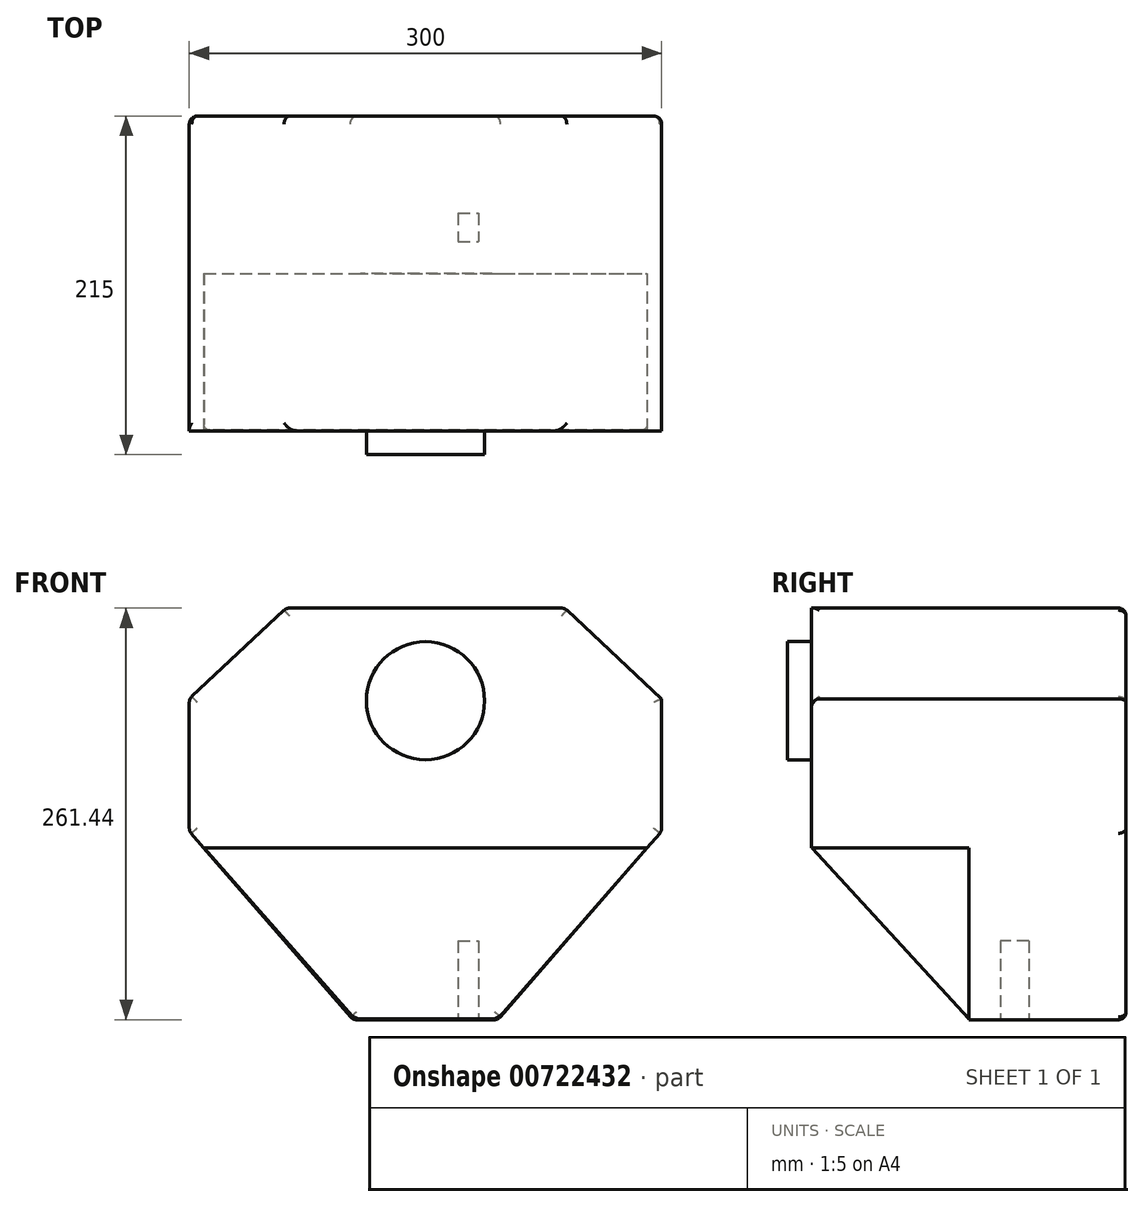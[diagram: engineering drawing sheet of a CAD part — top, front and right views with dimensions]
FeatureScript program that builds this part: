
annotation { "Feature Type Name" : "Feature", "Feature Type Description" : "" }
export const myFeature = defineFeature(function(context is Context, id is Id, definition is map)
    precondition{}
    {
        {
            var Q0;
            Q0=qCreatedBy(makeId("Front.planeOp"),FACE);
            var sketch = newSketch(context, id + "F0", { "sketchPlane" : qUnion([Q0])});
            skLineSegment(sketch, "E0.bottom", {"start": v(-150, -42) * mm, "end": v(150, -42) * mm});
            skLineSegment(sketch, "E0.top", {"start": v(-150, 42) * mm, "end": v(150, 42) * mm});
            skLineSegment(sketch, "E0.left", {"start": v(-150, -42) * mm, "end": v(-150, 42) * mm});
            skLineSegment(sketch, "E0.right", {"start": v(150, -42) * mm, "end": v(150, 42) * mm});
            skPoint(sketch, "E0.middle", {"position": v(0, 0) * mm});
            skLineSegment(sketch, "E1.bottom", {"start": v(-88.3, -15.66) * mm, "end": v(88.3, -15.66) * mm});
            skLineSegment(sketch, "E1.top", {"start": v(-88.3, 99.65) * mm, "end": v(88.3, 99.65) * mm});
            skLineSegment(sketch, "E1.left", {"start": v(-88.3, -15.66) * mm, "end": v(-88.3, 99.65) * mm});
            skLineSegment(sketch, "E1.right", {"start": v(88.3, -15.66) * mm, "end": v(88.3, 99.65) * mm});
            skPoint(sketch, "E1.middle", {"position": v(0, 42) * mm});
            skLineSegment(sketch, "E2.bottom", {"start": v(-46.14, -161.8) * mm, "end": v(46.14, -161.8) * mm});
            skLineSegment(sketch, "E2.top", {"start": v(-46.14, 77.8) * mm, "end": v(46.14, 77.8) * mm});
            skLineSegment(sketch, "E2.left", {"start": v(-46.14, -161.8) * mm, "end": v(-46.14, 77.8) * mm});
            skLineSegment(sketch, "E2.right", {"start": v(46.14, -161.8) * mm, "end": v(46.14, 77.8) * mm});
            skPoint(sketch, "E2.middle", {"position": v(0, -42) * mm});
            skLineSegment(sketch, "E3", {"start": v(-150, -42) * mm, "end": v(-46.14, -161.8) * mm});
            skLineSegment(sketch, "E4", {"start": v(46.14, -161.8) * mm, "end": v(150, -42) * mm});
            skLineSegment(sketch, "E5", {"start": v(-150, 42) * mm, "end": v(-88.3, 99.65) * mm});
            skLineSegment(sketch, "E6", {"start": v(150, 42) * mm, "end": v(88.3, 99.65) * mm});
            skSolve(sketch);
        }
        {
            var Q0;
            {var subQ0=sQuery(id+"F0.wireOp",EDGE,"E2.left");var subQ1=sQuery(id+"F0.wireOp",EDGE,"E0.top");var subQ2=makeQuery(id+"F0.imprint","INTERSECT",VERTEX,{"derivedFrom":[subQ1,subQ0]});Q0=makeQuery(id+"F0.imprint","IMPRINT",FACE,{"disambiguationData":[TD([[makeQuery(id+"F0.imprint","IMPRINT",EDGE,{"disambiguationData":[TD([[subQ2,-1.0]])],"derivedFrom":subQ1}),-1.0]])]});}
            var Q1;
            {var subQ0=sQuery(id+"F0.wireOp",EDGE,"E1.left");var subQ1=sQuery(id+"F0.wireOp",EDGE,"E0.top");var subQ2=makeQuery(id+"F0.imprint","INTERSECT",VERTEX,{"derivedFrom":[subQ1,subQ0]});Q1=makeQuery(id+"F0.imprint","IMPRINT",FACE,{"disambiguationData":[TD([[makeQuery(id+"F0.imprint","IMPRINT",EDGE,{"disambiguationData":[TD([[subQ2,-1.0]])],"derivedFrom":subQ1}),-1.0]])]});}
            var Q2;
            {var subQ0=sQuery(id+"F0.wireOp",EDGE,"E0.left");Q2=makeQuery(id+"F0.imprint","IMPRINT",FACE,{"disambiguationData":[TD([[makeQuery(id+"F0.imprint","IMPRINT",EDGE,{"derivedFrom":subQ0}),-1.0]])]});}
            var Q3;
            {var subQ0=sQuery(id+"F0.wireOp",EDGE,"E2.left");var subQ1=sQuery(id+"F0.wireOp",EDGE,"E0.bottom");var subQ2=makeQuery(id+"F0.imprint","INTERSECT",VERTEX,{"derivedFrom":[subQ1,subQ0]});Q3=makeQuery(id+"F0.imprint","IMPRINT",FACE,{"disambiguationData":[TD([[makeQuery(id+"F0.imprint","IMPRINT",EDGE,{"disambiguationData":[TD([[subQ2,-1.0]])],"derivedFrom":subQ1}),1.0]])]});}
            var Q4;
            {var subQ0=sQuery(id+"F0.wireOp",EDGE,"E0.right");Q4=makeQuery(id+"F0.imprint","IMPRINT",FACE,{"disambiguationData":[TD([[makeQuery(id+"F0.imprint","IMPRINT",EDGE,{"derivedFrom":subQ0}),1.0]])]});}
            var Q5;
            {var subQ0=sQuery(id+"F0.wireOp",EDGE,"E2.right");var subQ1=sQuery(id+"F0.wireOp",EDGE,"E0.top");var subQ2=makeQuery(id+"F0.imprint","INTERSECT",VERTEX,{"derivedFrom":[subQ1,subQ0]});Q5=makeQuery(id+"F0.imprint","IMPRINT",FACE,{"disambiguationData":[TD([[makeQuery(id+"F0.imprint","IMPRINT",EDGE,{"disambiguationData":[TD([[subQ2,-1.0]])],"derivedFrom":subQ1}),-1.0]])]});}
            var Q6;
            {var subQ0=sQuery(id+"F0.wireOp",EDGE,"E3");Q6=makeQuery(id+"F0.imprint","IMPRINT",FACE,{"disambiguationData":[TD([[makeQuery(id+"F0.imprint","IMPRINT",EDGE,{"derivedFrom":subQ0}),1.0]])]});}
            var Q7;
            {var subQ5=sQuery(id+"F0.wireOp",EDGE,"E2.bottom");Q7=makeQuery(id+"F0.imprint","IMPRINT",FACE,{"disambiguationData":[TD([[makeQuery(id+"F0.imprint","IMPRINT",EDGE,{"derivedFrom":subQ5}),1.0]])]});}
            var Q8;
            {var subQ0=sQuery(id+"F0.wireOp",EDGE,"E4");Q8=makeQuery(id+"F0.imprint","IMPRINT",FACE,{"disambiguationData":[TD([[makeQuery(id+"F0.imprint","IMPRINT",EDGE,{"derivedFrom":subQ0}),1.0]])]});}
            var Q9;
            {var subQ1=sQuery(id+"F0.wireOp",EDGE,"E1.top");Q9=makeQuery(id+"F0.imprint","IMPRINT",FACE,{"disambiguationData":[TD([[makeQuery(id+"F0.imprint","IMPRINT",EDGE,{"derivedFrom":subQ1}),-1.0]])]});}
            var Q10;
            {var subQ5=sQuery(id+"F0.wireOp",EDGE,"E2.top");Q10=makeQuery(id+"F0.imprint","IMPRINT",FACE,{"disambiguationData":[TD([[makeQuery(id+"F0.imprint","IMPRINT",EDGE,{"derivedFrom":subQ5}),-1.0]])]});}
            var Q11;
            {var subQ0=sQuery(id+"F0.wireOp",EDGE,"E5");Q11=makeQuery(id+"F0.imprint","IMPRINT",FACE,{"disambiguationData":[TD([[makeQuery(id+"F0.imprint","IMPRINT",EDGE,{"derivedFrom":subQ0}),-1.0]])]});}
            var Q12;
            {var subQ0=sQuery(id+"F0.wireOp",EDGE,"E6");Q12=makeQuery(id+"F0.imprint","IMPRINT",FACE,{"disambiguationData":[TD([[makeQuery(id+"F0.imprint","IMPRINT",EDGE,{"derivedFrom":subQ0}),1.0]])]});}
            extrude(context, id + "F1", {"entities" : qUnion([Q0, Q1, Q2, Q3, Q4, Q5, Q6, Q7, Q8, Q9, Q10, Q11, Q12]), "depth" : 100 * mm, "offsetDistance" : 25 * mm, "hasSecondDirection" : true, "secondDirectionOppositeDirection" : true, "secondDirectionDepth" : 100 * mm});
        }
        {
            var Q0;
            Q0=makeQuery(id+"F1.opExtrude","CAP_FACE",FACE,{"disambiguationData":[OSD([sQuery(id+"F0.wireOp",EDGE,"E0.left"),sQuery(id+"F0.wireOp",EDGE,"E0.right"),sQuery(id+"F0.wireOp",EDGE,"E1.top"),sQuery(id+"F0.wireOp",EDGE,"E2.bottom"),sQuery(id+"F0.wireOp",EDGE,"E3"),sQuery(id+"F0.wireOp",EDGE,"E4"),sQuery(id+"F0.wireOp",EDGE,"E5"),sQuery(id+"F0.wireOp",EDGE,"E6")])],"isStart":false});
            var sketch = newSketch(context, id + "F2", { "sketchPlane" : qUnion([Q0])});
            skLineSegment(sketch, "E7", {"start": v(-140.78, -52.63) * mm, "end": v(140.78, -52.63) * mm});
            skLineSegment(sketch, "E8", {"start": v(140.78, -52.63) * mm, "end": v(46.14, -161.8) * mm});
            skLineSegment(sketch, "E9", {"start": v(46.14, -161.8) * mm, "end": v(-46.14, -161.8) * mm});
            skLineSegment(sketch, "E10", {"start": v(-46.14, -161.8) * mm, "end": v(-140.78, -52.63) * mm});
            skSolve(sketch);
        }
        {
            var Q0;
            Q0=qSketchRegion(id+"F2",true);
            extrude(context, id + "F3", {"entities" : qUnion([Q0]), "operationType" : NewBodyOperationType.REMOVE, "oppositeDirection" : true, "depth" : 100 * mm, "offsetDistance" : 25 * mm});
        }
        {
            var Q0;
            Q0=qCreatedBy(makeId("Right.planeOp"),FACE);
            var sketch = newSketch(context, id + "F4", { "sketchPlane" : qUnion([Q0])});
            skLineSegment(sketch, "E11", {"start": v(0, -161.34) * mm, "end": v(-99.62, -52.57) * mm});
            skLineSegment(sketch, "E12", {"start": v(-99.62, -52.57) * mm, "end": v(0, -52.57) * mm});
            skLineSegment(sketch, "E13", {"start": v(0, -52.57) * mm, "end": v(0, -161.34) * mm});
            skSolve(sketch);
        }
        {
            var Q0;
            Q0=makeQuery(id+"F4.imprint","IMPRINT",FACE,{"disambiguationData":[TD([[makeQuery(id+"F4.imprint","IMPRINT",EDGE,{"derivedFrom":sQuery(id+"F4.wireOp",EDGE,"E11")}),-1.0]])]});
            extrude(context, id + "F5", {"entities" : qUnion([Q0]), "operationType" : NewBodyOperationType.ADD, "depth" : 150 * mm, "offsetDistance" : 25 * mm, "hasSecondDirection" : true, "secondDirectionOppositeDirection" : true, "secondDirectionDepth" : 150 * mm});
        }
        {
            var Q0;
            Q0=makeQuery(id+"F1.opExtrude","CAP_FACE",FACE,{"disambiguationData":[OSD([sQuery(id+"F0.wireOp",EDGE,"E0.left"),sQuery(id+"F0.wireOp",EDGE,"E0.right"),sQuery(id+"F0.wireOp",EDGE,"E1.top"),sQuery(id+"F0.wireOp",EDGE,"E2.bottom"),sQuery(id+"F0.wireOp",EDGE,"E3"),sQuery(id+"F0.wireOp",EDGE,"E4"),sQuery(id+"F0.wireOp",EDGE,"E5"),sQuery(id+"F0.wireOp",EDGE,"E6")])],"isStart":false});
            var sketch = newSketch(context, id + "F6", { "sketchPlane" : qUnion([Q0])});
            skLineSegment(sketch, "E14", {"start": v(-150, -42) * mm, "end": v(-44.71, -161.7) * mm});
            skLineSegment(sketch, "E15", {"start": v(-44.71, -161.7) * mm, "end": v(45.6, -161.7) * mm});
            skLineSegment(sketch, "E16", {"start": v(45.6, -161.7) * mm, "end": v(150, -42) * mm});
            skLineSegment(sketch, "E17", {"start": v(150, -42) * mm, "end": v(150, -161.7) * mm});
            skLineSegment(sketch, "E18", {"start": v(150, -161.7) * mm, "end": v(-150.56, -161.7) * mm});
            skLineSegment(sketch, "E19", {"start": v(-150.56, -161.7) * mm, "end": v(-150, -42) * mm});
            skSolve(sketch);
        }
        {
            var Q0;
            {var subQ1=sQuery(id+"F6.wireOp",EDGE,"E19");Q0=makeQuery(id+"F6.imprint","IMPRINT",FACE,{"disambiguationData":[TD([[makeQuery(id+"F6.imprint","IMPRINT",EDGE,{"derivedFrom":subQ1}),-1.0]])]});}
            var Q1;
            {var subQ1=sQuery(id+"F6.wireOp",EDGE,"E17");Q1=makeQuery(id+"F6.imprint","IMPRINT",FACE,{"disambiguationData":[TD([[makeQuery(id+"F6.imprint","IMPRINT",EDGE,{"derivedFrom":subQ1}),-1.0]])]});}
            extrude(context, id + "F7", {"entities" : qUnion([Q0, Q1]), "operationType" : NewBodyOperationType.REMOVE, "oppositeDirection" : true, "depth" : 100 * mm, "offsetDistance" : 25 * mm});
        }
        {
            var Q0;
            Q0=makeQuery(id+"F1.opExtrude","CAP_EDGE",EDGE,{"disambiguationData":[OSD([sQuery(id+"F0.wireOp",EDGE,"E1.top")])],"isStart":true});
            var Q1;
            Q1=makeQuery(id+"F1.opExtrude","CAP_EDGE",EDGE,{"disambiguationData":[OSD([sQuery(id+"F0.wireOp",EDGE,"E6")])],"isStart":true});
            var Q2;
            Q2=makeQuery(id+"F1.opExtrude","CAP_FACE",FACE,{"disambiguationData":[OSD([sQuery(id+"F0.wireOp",EDGE,"E0.left"),sQuery(id+"F0.wireOp",EDGE,"E0.right"),sQuery(id+"F0.wireOp",EDGE,"E1.top"),sQuery(id+"F0.wireOp",EDGE,"E2.bottom"),sQuery(id+"F0.wireOp",EDGE,"E3"),sQuery(id+"F0.wireOp",EDGE,"E4"),sQuery(id+"F0.wireOp",EDGE,"E5"),sQuery(id+"F0.wireOp",EDGE,"E6")])],"isStart":true});
            fillet(context, id + "F8", {"entities" : qUnion([Q0, Q1, Q2]), "radius" : 5 * mm, "tangentPropagation" : true, "allowEdgeOverflow" : false});
        }
        {
            var Q0;
            Q0=makeQuery(id+"F1.opExtrude","SWEPT_EDGE",EDGE,{"disambiguationData":[OSD([sQuery(id+"F0.wireOp",EDGE,"E0.bottom"),sQuery(id+"F0.wireOp",EDGE,"E0.right"),sQuery(id+"F0.wireOp",EDGE,"E4")])]});
            var Q1;
            Q1=makeQuery(id+"F7.boolean.opBoolean","INTERSECT",EDGE,{"derivedFrom":[makeQuery(id+"F5.opExtrude","SWEPT_FACE",FACE,{"disambiguationData":[OSD([sQuery(id+"F4.wireOp",EDGE,"E11")])]}),makeQuery(id+"F7.opExtrude","SWEPT_FACE",FACE,{"disambiguationData":[OSD([sQuery(id+"F6.wireOp",EDGE,"E16")])]})]});
            var Q2;
            Q2=makeQuery(id+"F1.opExtrude","SWEPT_EDGE",EDGE,{"disambiguationData":[OSD([sQuery(id+"F0.wireOp",EDGE,"E2.bottom"),sQuery(id+"F0.wireOp",EDGE,"E2.right"),sQuery(id+"F0.wireOp",EDGE,"E4")])]});
            var Q3;
            Q3=makeQuery(id+"F1.opExtrude","CAP_EDGE",EDGE,{"disambiguationData":[OSD([sQuery(id+"F0.wireOp",EDGE,"E6")])],"isStart":false});
            var Q4;
            Q4=makeQuery(id+"F1.opExtrude","SWEPT_EDGE",EDGE,{"disambiguationData":[OSD([sQuery(id+"F0.wireOp",EDGE,"E1.top"),sQuery(id+"F0.wireOp",EDGE,"E1.right"),sQuery(id+"F0.wireOp",EDGE,"E6")])]});
            var Q5;
            Q5=makeQuery(id+"F1.opExtrude","SWEPT_EDGE",EDGE,{"disambiguationData":[OSD([sQuery(id+"F0.wireOp",EDGE,"E1.top"),sQuery(id+"F0.wireOp",EDGE,"E1.left"),sQuery(id+"F0.wireOp",EDGE,"E5")])]});
            var Q6;
            Q6=makeQuery(id+"F1.opExtrude","CAP_EDGE",EDGE,{"disambiguationData":[OSD([sQuery(id+"F0.wireOp",EDGE,"E5")])],"isStart":false});
            var Q7;
            Q7=makeQuery(id+"F1.opExtrude","SWEPT_EDGE",EDGE,{"disambiguationData":[OSD([sQuery(id+"F0.wireOp",EDGE,"E0.top"),sQuery(id+"F0.wireOp",EDGE,"E0.left"),sQuery(id+"F0.wireOp",EDGE,"E5")])]});
            var Q8;
            Q8=makeQuery(id+"F1.opExtrude","SWEPT_EDGE",EDGE,{"disambiguationData":[OSD([sQuery(id+"F0.wireOp",EDGE,"E0.bottom"),sQuery(id+"F0.wireOp",EDGE,"E0.left"),sQuery(id+"F0.wireOp",EDGE,"E3")])]});
            var Q9;
            Q9=makeQuery(id+"F7.boolean.opBoolean","INTERSECT",EDGE,{"derivedFrom":[makeQuery(id+"F5.opExtrude","SWEPT_FACE",FACE,{"disambiguationData":[OSD([sQuery(id+"F4.wireOp",EDGE,"E11")])]}),makeQuery(id+"F7.opExtrude","SWEPT_FACE",FACE,{"disambiguationData":[OSD([sQuery(id+"F6.wireOp",EDGE,"E14")])]})]});
            var Q10;
            Q10=makeQuery(id+"F1.opExtrude","SWEPT_EDGE",EDGE,{"disambiguationData":[OSD([sQuery(id+"F0.wireOp",EDGE,"E2.bottom"),sQuery(id+"F0.wireOp",EDGE,"E2.left"),sQuery(id+"F0.wireOp",EDGE,"E3")])]});
            fillet(context, id + "F9", {"entities" : qUnion([Q0, Q1, Q2, Q3, Q4, Q5, Q6, Q7, Q8, Q9, Q10]), "radius" : 5 * mm, "tangentPropagation" : true, "allowEdgeOverflow" : false});
        }
        {
            var Q0;
            Q0=makeQuery(id+"F1.opExtrude","CAP_FACE",FACE,{"disambiguationData":[OSD([sQuery(id+"F0.wireOp",EDGE,"E0.left"),sQuery(id+"F0.wireOp",EDGE,"E0.right"),sQuery(id+"F0.wireOp",EDGE,"E1.top"),sQuery(id+"F0.wireOp",EDGE,"E2.bottom"),sQuery(id+"F0.wireOp",EDGE,"E3"),sQuery(id+"F0.wireOp",EDGE,"E4"),sQuery(id+"F0.wireOp",EDGE,"E5"),sQuery(id+"F0.wireOp",EDGE,"E6")])],"isStart":false});
            var sketch = newSketch(context, id + "F10", { "sketchPlane" : qUnion([Q0])});
            skCircle(sketch, "E20", {"center": v(0, 40.8) * mm, "radius": 37.5 * mm});
            skPoint(sketch, "E20.centerSnap0", {"position": v(0, -52.63) * mm});
            skSolve(sketch);
        }
        {
            var Q0;
            Q0=makeQuery(id+"F10.imprint","IMPRINT",FACE,{"disambiguationData":[TD([[makeQuery(id+"F10.imprint","IMPRINT",EDGE,{"derivedFrom":sQuery(id+"F10.wireOp",EDGE,"E20")}),1.0]])]});
            var Q1;
            Q1=sQuery(id+"F10.wireOp",EDGE,"E20");
            extrude(context, id + "F11", {"entities" : qUnion([Q0]), "operationType" : NewBodyOperationType.ADD, "surfaceEntities" : qUnion([Q1]), "depth" : 15 * mm, "offsetDistance" : 25 * mm});
        }
        {
            var Q0;
            Q0=makeQuery(id+"F1.opExtrude","SWEPT_FACE",FACE,{"disambiguationData":[OSD([sQuery(id+"F0.wireOp",EDGE,"E2.bottom")])]});
            var sketch = newSketch(context, id + "F12", { "sketchPlane" : qUnion([Q0])});
            skLineSegment(sketch, "E21.bottom", {"start": v(20.82, -38.24) * mm, "end": v(33.67, -38.24) * mm});
            skLineSegment(sketch, "E21.top", {"start": v(20.82, -20.25) * mm, "end": v(33.67, -20.25) * mm});
            skLineSegment(sketch, "E21.left", {"start": v(20.82, -38.24) * mm, "end": v(20.82, -20.25) * mm});
            skLineSegment(sketch, "E21.right", {"start": v(33.67, -38.24) * mm, "end": v(33.67, -20.25) * mm});
            skPoint(sketch, "E21.middle", {"position": v(27.24, -29.25) * mm});
            skSolve(sketch);
        }
        {
            var Q0;
            Q0=qSketchRegion(id+"F12",true);
            extrude(context, id + "F13", {"entities" : qUnion([Q0]), "operationType" : NewBodyOperationType.REMOVE, "oppositeDirection" : true, "depth" : 50 * mm, "offsetDistance" : 25 * mm});
        }
    });
